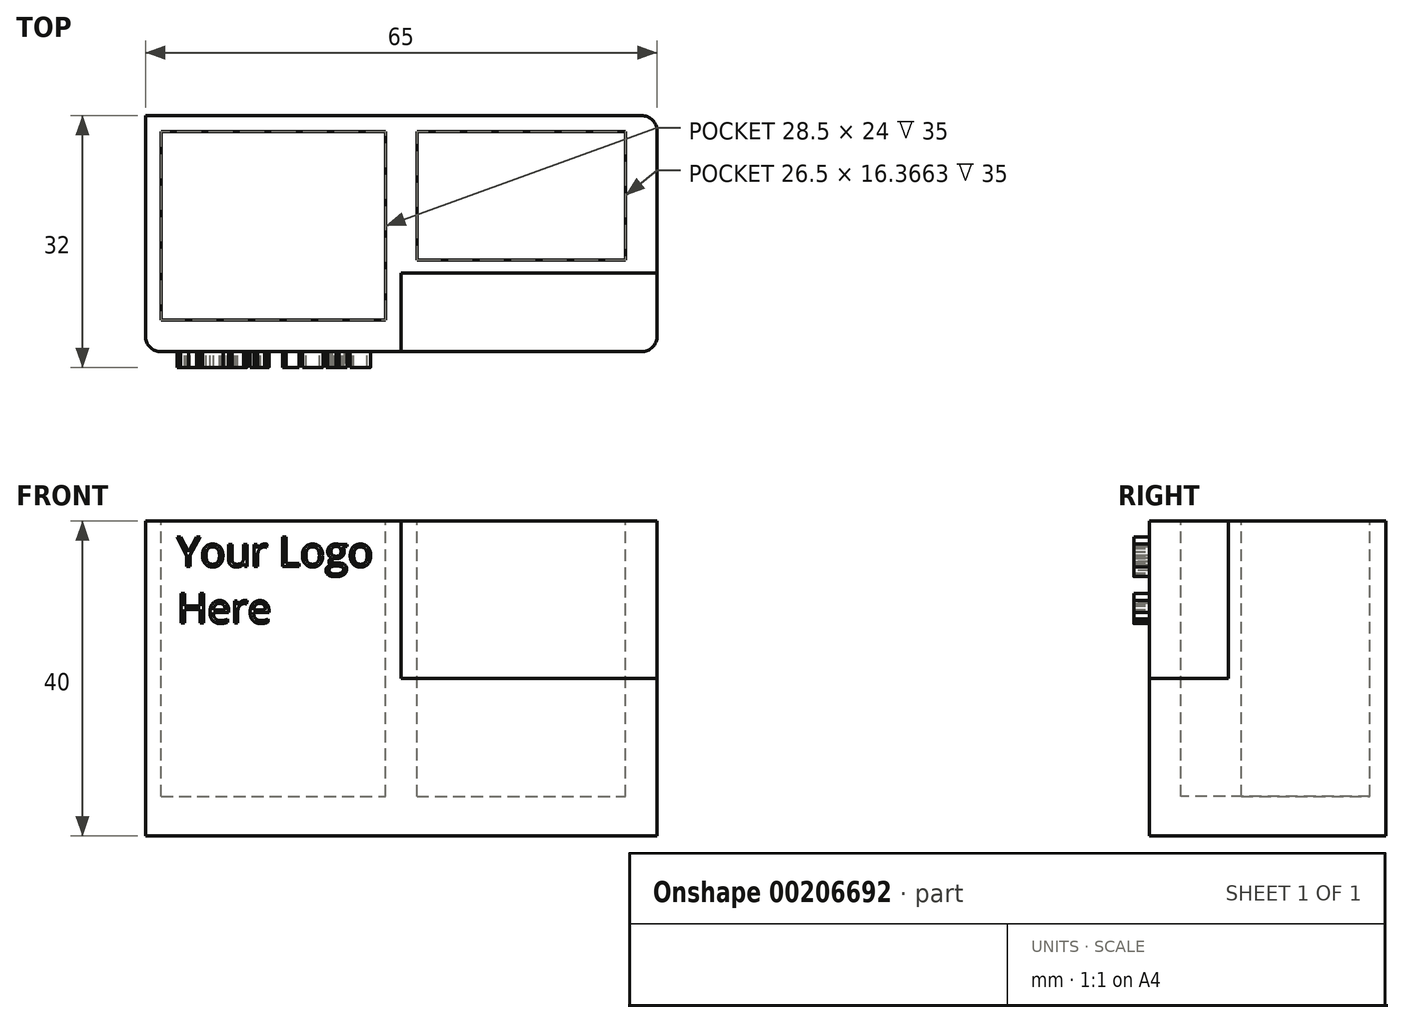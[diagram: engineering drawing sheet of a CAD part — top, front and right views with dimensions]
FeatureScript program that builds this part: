
annotation { "Feature Type Name" : "Feature", "Feature Type Description" : "" }
export const myFeature = defineFeature(function(context is Context, id is Id, definition is map)
    precondition{}
    {
        {
            var Q0;
            Q0=qCreatedBy(makeId("Top.planeOp"),FACE);
            var sketch = newSketch(context, id + "F0", { "sketchPlane" : qUnion([Q0])});
            skLineSegment(sketch, "E0.bottom", {"start": v(-25.97, 14.21) * mm, "end": v(39.03, 14.21) * mm});
            skLineSegment(sketch, "E0.top", {"start": v(-25.97, -15.79) * mm, "end": v(39.03, -15.79) * mm});
            skLineSegment(sketch, "E0.left", {"start": v(-25.97, 14.21) * mm, "end": v(-25.97, -15.79) * mm});
            skLineSegment(sketch, "E0.right", {"start": v(39.03, 14.21) * mm, "end": v(39.03, -15.79) * mm});
            skSolve(sketch);
        }
        {
            var Q0;
            Q0 = qSketchRegion(id + "F0", true);
            extrude(context, id + "F1", {"entities" : qUnion([Q0]), "depth" : 40 * mm});
        }
        {
            var Q0;
            Q0=makeQuery(id+"F1.opExtrude","SWEPT_FACE",FACE,{"disambiguationData":[OSD([sQuery(id+"F0.wireOp",EDGE,"E0.top")])]});
            var sketch = newSketch(context, id + "F2", { "sketchPlane" : qUnion([Q0])});
            skLineSegment(sketch, "E1", {"start": v(6.53, 0) * mm, "end": v(6.53, 40) * mm});
            skLineSegment(sketch, "E2", {"start": v(6.53, 20) * mm, "end": v(39.03, 20) * mm});
            skSolve(sketch);
        }
        {
            var Q0;
            {var subQ4=sQuery(id+"F2.wireOp",EDGE,"E2");Q0=makeQuery(id+"F2.imprint","IMPRINT",FACE,{"disambiguationData":[TD([[makeQuery(id+"F2.imprint","IMPRINT",EDGE,{"derivedFrom":subQ4}),1.0]])]});}
            extrude(context, id + "F3", {"entities" : qUnion([Q0]), "operationType" : NewBodyOperationType.REMOVE, "oppositeDirection" : true, "depth" : 10 * mm});
        }
        {
            var Q0;
            Q0=makeQuery(id+"F1.opExtrude","SWEPT_EDGE",EDGE,{"disambiguationData":[OSD([sQuery(id+"F0.wireOp",EDGE,"E0.top"),sQuery(id+"F0.wireOp",EDGE,"E0.right")])]});
            var Q1;
            Q1=makeQuery(id+"F1.opExtrude","SWEPT_EDGE",EDGE,{"disambiguationData":[OSD([sQuery(id+"F0.wireOp",EDGE,"E0.bottom"),sQuery(id+"F0.wireOp",EDGE,"E0.right")])]});
            var Q2;
            Q2=makeQuery(id+"F1.opExtrude","SWEPT_EDGE",EDGE,{"disambiguationData":[OSD([sQuery(id+"F0.wireOp",EDGE,"E0.top"),sQuery(id+"F0.wireOp",EDGE,"E0.left")])]});
            fillet(context, id + "F4", {"entities" : qUnion([Q0, Q1, Q2]), "radius" : 2 * mm, "tangentPropagation" : true, "allowEdgeOverflow" : false});
        }
        {
            var Q0;
            Q0=makeQuery(id+"F1.opExtrude","CAP_FACE",FACE,{"disambiguationData":[OSD([sQuery(id+"F0.wireOp",EDGE,"E0.bottom"),sQuery(id+"F0.wireOp",EDGE,"E0.top"),sQuery(id+"F0.wireOp",EDGE,"E0.left"),sQuery(id+"F0.wireOp",EDGE,"E0.right")])],"isStart":false});
            var sketch = newSketch(context, id + "F5", { "sketchPlane" : qUnion([Q0])});
            skLineSegment(sketch, "E3.bottom", {"start": v(-23.97, 12.21) * mm, "end": v(4.53, 12.21) * mm});
            skLineSegment(sketch, "E3.top", {"start": v(-23.97, -11.79) * mm, "end": v(4.53, -11.79) * mm});
            skLineSegment(sketch, "E3.left", {"start": v(-23.97, 12.21) * mm, "end": v(-23.97, -11.79) * mm});
            skLineSegment(sketch, "E3.right", {"start": v(4.53, 12.21) * mm, "end": v(4.53, -11.79) * mm});
            skLineSegment(sketch, "E4.bottom", {"start": v(8.53, -4.16) * mm, "end": v(35.03, -4.16) * mm});
            skLineSegment(sketch, "E4.top", {"start": v(8.53, 12.21) * mm, "end": v(35.03, 12.21) * mm});
            skLineSegment(sketch, "E4.left", {"start": v(8.53, -4.16) * mm, "end": v(8.53, 12.21) * mm});
            skLineSegment(sketch, "E4.right", {"start": v(35.03, -4.16) * mm, "end": v(35.03, 12.21) * mm});
            skSolve(sketch);
        }
        {
            var Q0;
            Q0=makeQuery(id+"F5.imprint","IMPRINT",FACE,{"disambiguationData":[TD([[makeQuery(id+"F5.imprint","IMPRINT",EDGE,{"derivedFrom":sQuery(id+"F5.wireOp",EDGE,"E3.bottom")}),-1.0]])]});
            extrude(context, id + "F6", {"entities" : qUnion([Q0]), "operationType" : NewBodyOperationType.REMOVE, "oppositeDirection" : true, "depth" : 35 * mm});
        }
        {
            var Q0;
            Q0=makeQuery(id+"F5.imprint","IMPRINT",FACE,{"disambiguationData":[TD([[makeQuery(id+"F5.imprint","IMPRINT",EDGE,{"derivedFrom":sQuery(id+"F5.wireOp",EDGE,"E4.bottom")}),1.0]])]});
            extrude(context, id + "F7", {"entities" : qUnion([Q0]), "operationType" : NewBodyOperationType.REMOVE, "oppositeDirection" : true, "depth" : 35 * mm});
        }
        {
            var Q0;
            Q0=makeQuery(id+"F1.opExtrude","SWEPT_FACE",FACE,{"disambiguationData":[OSD([sQuery(id+"F0.wireOp",EDGE,"E0.top")])]});
            var sketch = newSketch(context, id + "F8", { "sketchPlane" : qUnion([Q0])});
            skText(sketch, "E5", { "text": "Your Logo\nHere", "fontName": "OpenSans-Regular.ttf"});
            const initialGuessF8  = {"E5": [-0.02197, 0.0342, 1, 0, 0.0038]};
            skSetInitialGuess(sketch, initialGuessF8);
            skSolve(sketch);
        }
        {
            var Q0;
            Q0 = qSketchRegion(id + "F8", true);
            extrude(context, id + "F9", {"entities" : qUnion([Q0]), "operationType" : NewBodyOperationType.ADD, "depth" : 2 * mm});
        }
    });
